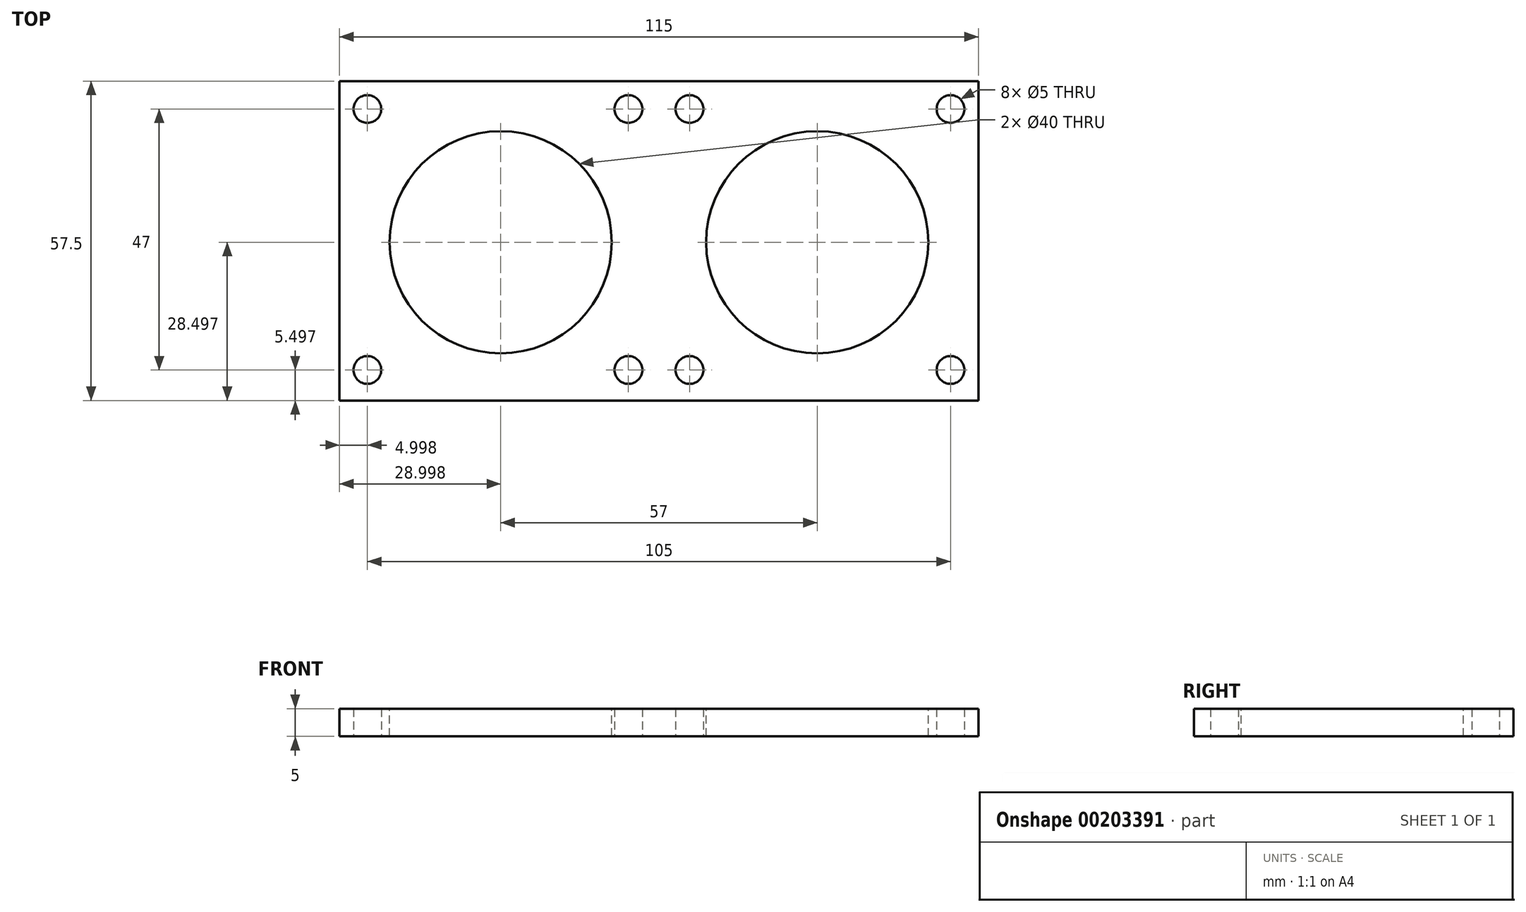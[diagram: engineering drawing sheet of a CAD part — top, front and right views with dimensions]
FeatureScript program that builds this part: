
annotation { "Feature Type Name" : "Feature", "Feature Type Description" : "" }
export const myFeature = defineFeature(function(context is Context, id is Id, definition is map)
    precondition{}
    {
        {
            var Q0;
            Q0=qCreatedBy(makeId("Top.planeOp"),FACE);
            var sketch = newSketch(context, id + "F0", { "sketchPlane" : qUnion([Q0])});
            skLineSegment(sketch, "E0.bottom", {"start": v(-26.34, 39.25) * mm, "end": v(31.16, 39.25) * mm});
            skLineSegment(sketch, "E0.top", {"start": v(-26.34, -18.25) * mm, "end": v(31.16, -18.25) * mm});
            skLineSegment(sketch, "E0.left", {"start": v(-26.34, 39.25) * mm, "end": v(-26.34, -18.25) * mm});
            skLineSegment(sketch, "E0.right", {"start": v(31.16, 39.25) * mm, "end": v(31.16, -18.25) * mm});
            skLineSegment(sketch, "E1.bottom", {"start": v(-20.84, 34.25) * mm, "end": v(26.16, 34.25) * mm, "construction": true});
            skLineSegment(sketch, "E1.top", {"start": v(-20.84, -12.75) * mm, "end": v(26.16, -12.75) * mm, "construction": true});
            skLineSegment(sketch, "E1.left", {"start": v(-20.84, 34.25) * mm, "end": v(-20.84, -12.75) * mm, "construction": true});
            skLineSegment(sketch, "E1.right", {"start": v(26.16, 34.25) * mm, "end": v(26.16, -12.75) * mm, "construction": true});
            skCircle(sketch, "E2", {"center": v(-20.84, -12.75) * mm, "radius": 2.5 * mm});
            skCircle(sketch, "E3", {"center": v(26.16, -12.75) * mm, "radius": 2.5 * mm});
            skCircle(sketch, "E4", {"center": v(26.16, 34.25) * mm, "radius": 2.5 * mm});
            skCircle(sketch, "E5", {"center": v(-20.84, 34.25) * mm, "radius": 2.5 * mm});
            skSolve(sketch);
        }
        {
            var Q0;
            Q0=makeQuery(id+"F0.imprint","IMPRINT",FACE,{"disambiguationData":[TD([[makeQuery(id+"F0.imprint","IMPRINT",EDGE,{"derivedFrom":sQuery(id+"F0.wireOp",EDGE,"E0.bottom")}),-1.0]])]});
            extrude(context, id + "F1", {"entities" : qUnion([Q0]), "depth" : 5 * mm, "offsetDistance" : 25 * mm});
        }
        {
            var Q0;
            Q0=makeQuery(id+"F1.opExtrude","CAP_FACE",FACE,{"disambiguationData":[OSD([sQuery(id+"F0.wireOp",EDGE,"E0.bottom"),sQuery(id+"F0.wireOp",EDGE,"E0.top"),sQuery(id+"F0.wireOp",EDGE,"E0.left"),sQuery(id+"F0.wireOp",EDGE,"E0.right"),sQuery(id+"F0.wireOp",EDGE,"E2"),sQuery(id+"F0.wireOp",EDGE,"E3"),sQuery(id+"F0.wireOp",EDGE,"E4"),sQuery(id+"F0.wireOp",EDGE,"E5")])],"isStart":false});
            var sketch = newSketch(context, id + "F2", { "sketchPlane" : qUnion([Q0])});
            skCircle(sketch, "E6", {"center": v(2.16, 10.25) * mm, "radius": 20 * mm});
            skSolve(sketch);
        }
        {
            var Q0;
            Q0 = qSketchRegion(id + "F2", true);
            extrude(context, id + "F3", {"entities" : qUnion([Q0]), "operationType" : NewBodyOperationType.REMOVE, "oppositeDirection" : true, "depth" : 5 * mm, "offsetDistance" : 25 * mm});
        }
        {
            var Q0;
            Q0=makeQuery(id+"F1.opExtrude","SWEPT_BODY",BODY,{"disambiguationData":[OSD([sQuery(id+"F0.wireOp",EDGE,"E0.bottom"),sQuery(id+"F0.wireOp",EDGE,"E0.top"),sQuery(id+"F0.wireOp",EDGE,"E0.left"),sQuery(id+"F0.wireOp",EDGE,"E0.right"),sQuery(id+"F0.wireOp",EDGE,"E2"),sQuery(id+"F0.wireOp",EDGE,"E3"),sQuery(id+"F0.wireOp",EDGE,"E4"),sQuery(id+"F0.wireOp",EDGE,"E5")])]});
            var Q1;
            Q1=makeQuery(id+"F1.opExtrude","SWEPT_FACE",FACE,{"disambiguationData":[OSD([sQuery(id+"F0.wireOp",EDGE,"E0.left")])]});
            mirror(context, id + "F4", {"operationType" : NewBodyOperationType.ADD, "entities" : qUnion([Q0]), "mirrorPlane" : qUnion([Q1])});
        }
    });
